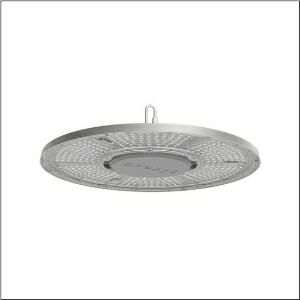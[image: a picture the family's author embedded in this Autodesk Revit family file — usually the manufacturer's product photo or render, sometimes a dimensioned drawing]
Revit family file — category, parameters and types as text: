
# Revit family: highbay_31-l_51hc42da4jmb
name_source: partatom
category: Lighting Fixtures
units: mm (PartAtom-declared; Revit-internal decimal feet)

## family parameters
Cut with Voids When Loaded = No
Host = Face
Light Source = No
Part Type = Normal
Room Calculation Point = No
Round Connector Dimension = Use Diameter
Shared = No

## types (1)
- Highbay 31-L (1 x LED, 20000 lm, 134 W, 4000K)
    Apparent Load = 134 VA
    CIE Flux Codes = 77 99 100 100 100
    Color Rendering = 80
    Color Temperature = 4000K
    Default Elevation = 1800 mm
    Description = Highbay 31-L, high bay luminaire, primary light control with lens, of PC, primary optical cover: cover panel, of PC, transparent, light emission: direct distribution, primary light characteristic: rotationally symmetric, installation type: suspended mounting, surface-mounted, LED, rated luminous flux: 20.000lm, luminous efficacy: 150lm/W, light colour: 840, colour temperature: 4000K, control gear: DALI 2, with cable, 5x 1.0mm², free wire ends, mains connection: 220..240V, AC, 50/60Hz, cable length: 1,5m, rated input power: 134W, housing, rotationally symmetric, of diecast aluminium, powder-coated, grey aluminium (RAL 9007), with hook on luminaire side, incl. screw, diameter: 404mm, protection rating (complete): IP65, insulation class (complete): insulation class I (protective earthing), certification: CE, ENEC, UKCA, protection symbol: D, impact resistance: IK08, permissible operating ambient temperature: -30..+45°C, corresponds to IFS (International Featured Standards) requirements for safety and quality in the food industry, packaging unit: 1 piece
    Height = 141 mm
    Lamp = 1 x LED
    Lamp Light Flux = 20000 lm
    Lamp Power = 134 W
    Lamp count = 1
    Length = 406 mm
    Luminous efficacy = 149 lm/W
    Manufacturer = Siteco
    ModVariant = No
    Model = 51HC42DA4JMB
    Mounting Place = Ceiling
    Mounting Type = Pendant
    Number of Poles = 1
    OnlyDefault = Yes
    Power Factor = 1
    Product Name = Highbay 31-L
    Product group = high bay luminaire
    ProductGroupID = 902
    Protection Class = Protection class I
    Protection Degree = IP 65
    RLX_Detail_Level = 1
    RLX_Emergency_Light_Flux = 0 lm
    RLX_Emergency_Type = 0
    RLX_Emergency_Type_DB = No
    RlxData = <blob elided: 172725 chars, md5=a645b874>
    Socket = socket
    Standby Power = 0 W
    System Light Flux = 20000 lm
    System Power = 134 W
    Type Comments = Product without accessories
    Type Image = l_1003610.jpg
    URL = http://relux.com
    VarID = ---
    Voltage = 0 V
    Weight = 0.00 kg
    Width = 0 mm  [stored 0 ft]

note: [stored X ft] marks values corroborated as IEEE doubles in the binary element streams (Revit-internal decimal feet)

## geometry (parser evidence)
native form markers: Blend x4, Sweep x9
no freeform markers — native parametric forms only
